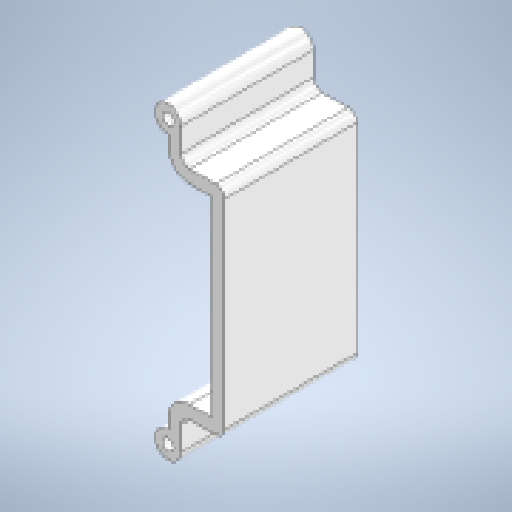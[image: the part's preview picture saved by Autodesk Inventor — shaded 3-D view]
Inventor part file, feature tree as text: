
AUTODESK INVENTOR PART (.ipt)
format: ipt  version: 2025.1 (Build 291241000, 241)  size: 175,104 bytes
history: native  units: mm
features: other x5, sketch x1, extrude x1, reference x1
ambient origin geometry x8: Origin, YZ Plane, XZ Plane, XY Plane, X Axis, Y Axis, Z Axis, Center Point
bodies: Body1 (feature_tree)
feature tree (8):
  other  "ソリッド1"
  sketch  "スケッチ1"
  other  "作業平面1"
  extrude  "押し出し1"  Depth=6.0mm
  reference  "参照1"
  other  "<userpath>\Documents\Inventor\Vixen\doutai.iam"
  other  "doutai.iam"
  other  "kataue:1"
